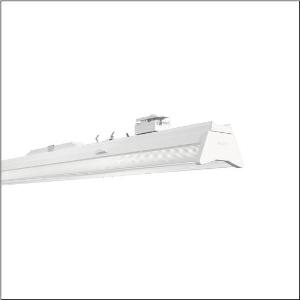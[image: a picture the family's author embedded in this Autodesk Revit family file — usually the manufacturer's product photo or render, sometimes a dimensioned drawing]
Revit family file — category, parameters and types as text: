
# Revit family: licross_r__11_performance_mo_51tm167n485g_4c90
name_source: partatom
category: Lighting Fixtures
units: mm (PartAtom-declared; Revit-internal decimal feet)

## family parameters
Cut with Voids When Loaded = No
Host = Face
Light Source = No
Part Type = Normal
Room Calculation Point = No
Round Connector Dimension = Use Diameter
Shared = No

## types (1)
- Licross® 11 Performance MO (1 x LED, 8840 lm, 48.6 W, 4000K)
    Apparent Load = 49 VA
    CIE Flux Codes = 66 88 96 79 100
    Color Rendering = 80
    Color Temperature = 4000K
    Default Elevation = 1800 mm
    Description = Licross® 11 Performance MO, luminaire insert, of sheet steel, galvanised, coil coated, white, length: 1.500mm, width: 120mm, height: 123mm, LED rated luminous flux: 8.840lm, light colour: 840, control gear: ON/OFF, with plug, 3-pole, with phase selection, mains connection: 220..240V, AC, 50/60Hz, rated input power: 49W, halogen-free wiring, primary light control with lens, of plastic, primary optical cover: cover, of PMMA, light emission: direct/indirect distribution, primary light characteristic: symmetric, protection rating (complete): IP40, insulation class (complete): insulation class I (protective earthing), certification: CE, ENEC, VDE, UKCA, protection symbol: D if used in an environment without relevant dust loads with corresponding accessories, impact resistance: IK06, permissible ambient temperature for indoor applications: -25..+35°C, corresponds to IFS (International Featured Standards) requirements for safety and quality in the food industry, reducing of maximum allowable ambient temperature of 5°C with ceiling mounting, LABS conformity tested according to VDMA 24364:2018-05, packaging unit: 1 piece
    Height = 114 mm
    Lamp = 1 x LED
    Lamp Light Flux = 8840 lm
    Lamp Power = 48.6 W
    Lamp count = 1
    Length = 1500 mm
    Luminous efficacy = 182 lm/W
    Manufacturer = Siteco
    ModVariant = No
    Model = 51TM167N485G
    Mounting Place = Ceiling
    Mounting Type = Pendant
    Number of Poles = 1
    OnlyDefault = Yes
    Power Factor = 1
    Product Name = Licross® 11 Performance MO
    Product group = luminaire insert
    ProductGroupID = 901
    Protection Class = Protection class I
    Protection Degree = IP 40
    RLX_Detail_Level = 1
    RLX_Emergency_Light_Flux = 0 lm
    RLX_Emergency_Type = 0
    RLX_Emergency_Type_DB = No
    RlxData = <blob elided: 30393 chars, md5=b418bdbf>
    Socket = socket
    Standby Power = 0 W
    System Light Flux = 8840 lm
    System Power = 49 W
    Type Comments = Product without accessories
    Type Image = l_1256138.jpg
    URL = http://relux.com
    VarID = ---
    Voltage = 0 V
    Weight = 0.00 kg
    Width = 120 mm

## geometry (parser evidence)
native form markers: Blend x4, Sweep x10
no freeform markers — native parametric forms only
